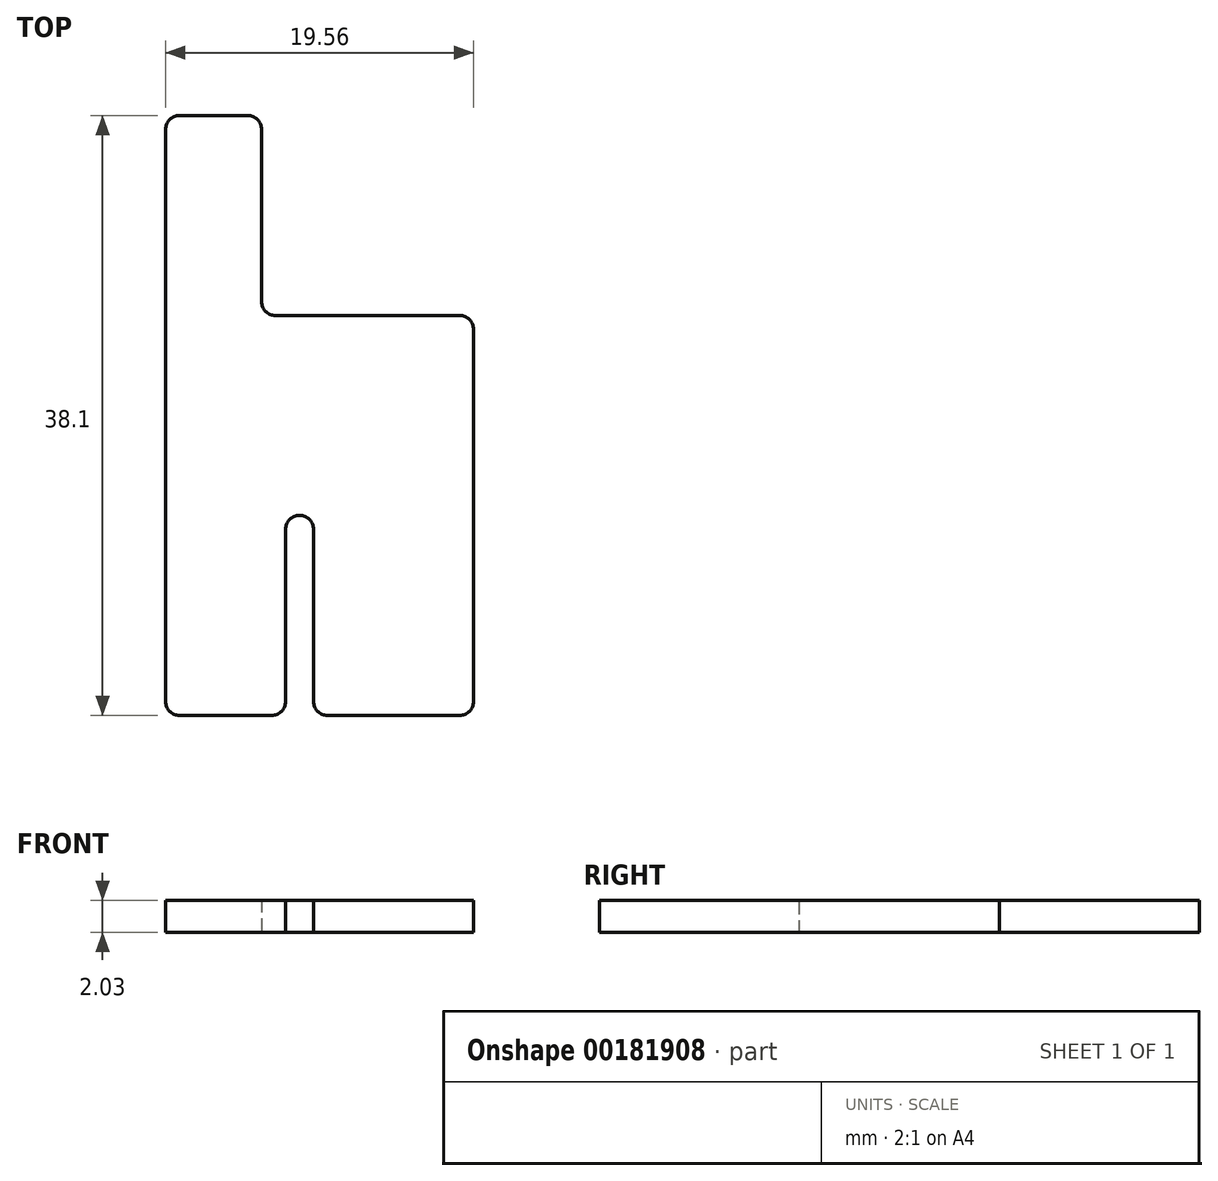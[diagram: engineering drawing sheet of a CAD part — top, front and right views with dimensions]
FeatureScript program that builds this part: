
annotation { "Feature Type Name" : "Feature", "Feature Type Description" : "" }
export const myFeature = defineFeature(function(context is Context, id is Id, definition is map)
    precondition{}
    {
        {
            var Q0;
            Q0=qCreatedBy(makeId("Top.planeOp"),FACE);
            var sketch = newSketch(context, id + "F0", { "sketchPlane" : qUnion([Q0])});
            skLineSegment(sketch, "E0", {"start": v(-7.62, 19.05) * mm, "end": v(-7.62, -19.05) * mm});
            skLineSegment(sketch, "E1", {"start": v(-7.62, -19.05) * mm, "end": v(0, -19.05) * mm});
            skLineSegment(sketch, "E2", {"start": v(0, -19.05) * mm, "end": v(0, -6.35) * mm});
            skLineSegment(sketch, "E3", {"start": v(0, -6.35) * mm, "end": v(1.78, -6.35) * mm});
            skLineSegment(sketch, "E4", {"start": v(1.78, -6.35) * mm, "end": v(1.78, -19.05) * mm});
            skLineSegment(sketch, "E5", {"start": v(1.78, -19.05) * mm, "end": v(11.94, -19.05) * mm});
            skLineSegment(sketch, "E6", {"start": v(11.94, -19.05) * mm, "end": v(11.94, 6.35) * mm});
            skLineSegment(sketch, "E7", {"start": v(11.94, 6.35) * mm, "end": v(-1.52, 6.35) * mm});
            skLineSegment(sketch, "E8", {"start": v(-1.52, 6.35) * mm, "end": v(-1.52, 19.05) * mm});
            skLineSegment(sketch, "E9", {"start": v(-1.52, 19.05) * mm, "end": v(-7.62, 19.05) * mm});
            skPoint(sketch, "E10", {"position": v(-7.62, 0) * mm});
            skSolve(sketch);
        }
        {
            var Q0;
            Q0 = qSketchRegion(id + "F0", true);
            extrude(context, id + "F1", {"entities" : qUnion([Q0]), "depth" : 2.03 * mm});
        }
        {
            var Q0;
            Q0=makeQuery(id+"F1.opExtrude","SWEPT_EDGE",EDGE,{"disambiguationData":[OSD([sQuery(id+"F0.wireOp",EDGE,"E0"),sQuery(id+"F0.wireOp",EDGE,"E1")])]});
            var Q1;
            Q1=makeQuery(id+"F1.opExtrude","SWEPT_EDGE",EDGE,{"disambiguationData":[OSD([sQuery(id+"F0.wireOp",EDGE,"E1"),sQuery(id+"F0.wireOp",EDGE,"E2")])]});
            var Q2;
            Q2=makeQuery(id+"F1.opExtrude","SWEPT_EDGE",EDGE,{"disambiguationData":[OSD([sQuery(id+"F0.wireOp",EDGE,"E2"),sQuery(id+"F0.wireOp",EDGE,"E3")])]});
            var Q3;
            Q3=makeQuery(id+"F1.opExtrude","SWEPT_EDGE",EDGE,{"disambiguationData":[OSD([sQuery(id+"F0.wireOp",EDGE,"E4"),sQuery(id+"F0.wireOp",EDGE,"E5")])]});
            var Q4;
            Q4=makeQuery(id+"F1.opExtrude","SWEPT_EDGE",EDGE,{"disambiguationData":[OSD([sQuery(id+"F0.wireOp",EDGE,"E5"),sQuery(id+"F0.wireOp",EDGE,"E6")])]});
            var Q5;
            Q5=makeQuery(id+"F1.opExtrude","SWEPT_EDGE",EDGE,{"disambiguationData":[OSD([sQuery(id+"F0.wireOp",EDGE,"E6"),sQuery(id+"F0.wireOp",EDGE,"E7")])]});
            var Q6;
            Q6=makeQuery(id+"F1.opExtrude","SWEPT_EDGE",EDGE,{"disambiguationData":[OSD([sQuery(id+"F0.wireOp",EDGE,"E8"),sQuery(id+"F0.wireOp",EDGE,"E9")])]});
            var Q7;
            Q7=makeQuery(id+"F1.opExtrude","SWEPT_EDGE",EDGE,{"disambiguationData":[OSD([sQuery(id+"F0.wireOp",EDGE,"E3"),sQuery(id+"F0.wireOp",EDGE,"E4")])]});
            var Q8;
            Q8=makeQuery(id+"F1.opExtrude","SWEPT_EDGE",EDGE,{"disambiguationData":[OSD([sQuery(id+"F0.wireOp",EDGE,"E0"),sQuery(id+"F0.wireOp",EDGE,"E9")])]});
            var Q9;
            Q9=makeQuery(id+"F1.opExtrude","SWEPT_EDGE",EDGE,{"disambiguationData":[OSD([sQuery(id+"F0.wireOp",EDGE,"E7"),sQuery(id+"F0.wireOp",EDGE,"E8")])]});
            fillet(context, id + "F2", {"entities" : qUnion([Q0, Q1, Q2, Q3, Q4, Q5, Q6, Q7, Q8, Q9]), "radius" : 0.89 * mm, "tangentPropagation" : true, "allowEdgeOverflow" : false});
        }
    });
